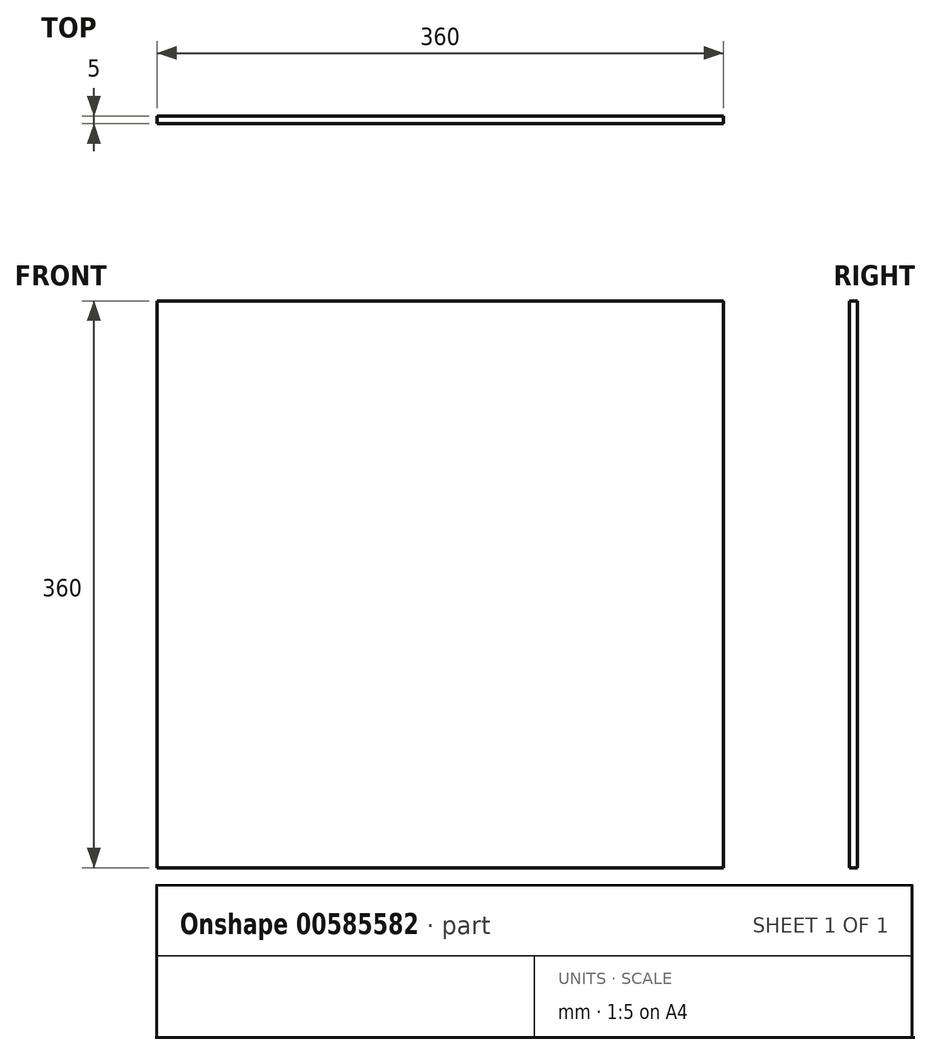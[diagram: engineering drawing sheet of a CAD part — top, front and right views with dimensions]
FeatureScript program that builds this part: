
annotation { "Feature Type Name" : "Feature", "Feature Type Description" : "" }
export const myFeature = defineFeature(function(context is Context, id is Id, definition is map)
    precondition{}
    {
        {
            var Q0;
            Q0=qCreatedBy(makeId("Front.planeOp"),FACE);
            var sketch = newSketch(context, id + "F0", { "sketchPlane" : qUnion([Q0])});
            skLineSegment(sketch, "E0.bottom", {"start": v(0, 0) * mm, "end": v(360, 0) * mm});
            skLineSegment(sketch, "E0.top", {"start": v(0, 360) * mm, "end": v(360, 360) * mm});
            skLineSegment(sketch, "E0.left", {"start": v(0, 0) * mm, "end": v(0, 360) * mm});
            skLineSegment(sketch, "E0.right", {"start": v(360, 0) * mm, "end": v(360, 360) * mm});
            skSolve(sketch);
        }
        {
            var Q0;
            Q0=makeQuery(id+"F0.imprint","IMPRINT",FACE,{"disambiguationData":[TD([[makeQuery(id+"F0.imprint","IMPRINT",EDGE,{"derivedFrom":sQuery(id+"F0.wireOp",EDGE,"E0.bottom")}),1.0]])]});
            extrude(context, id + "F1", {"entities" : qUnion([Q0]), "depth" : 5 * mm, "offsetDistance" : 25 * mm});
        }
    });
